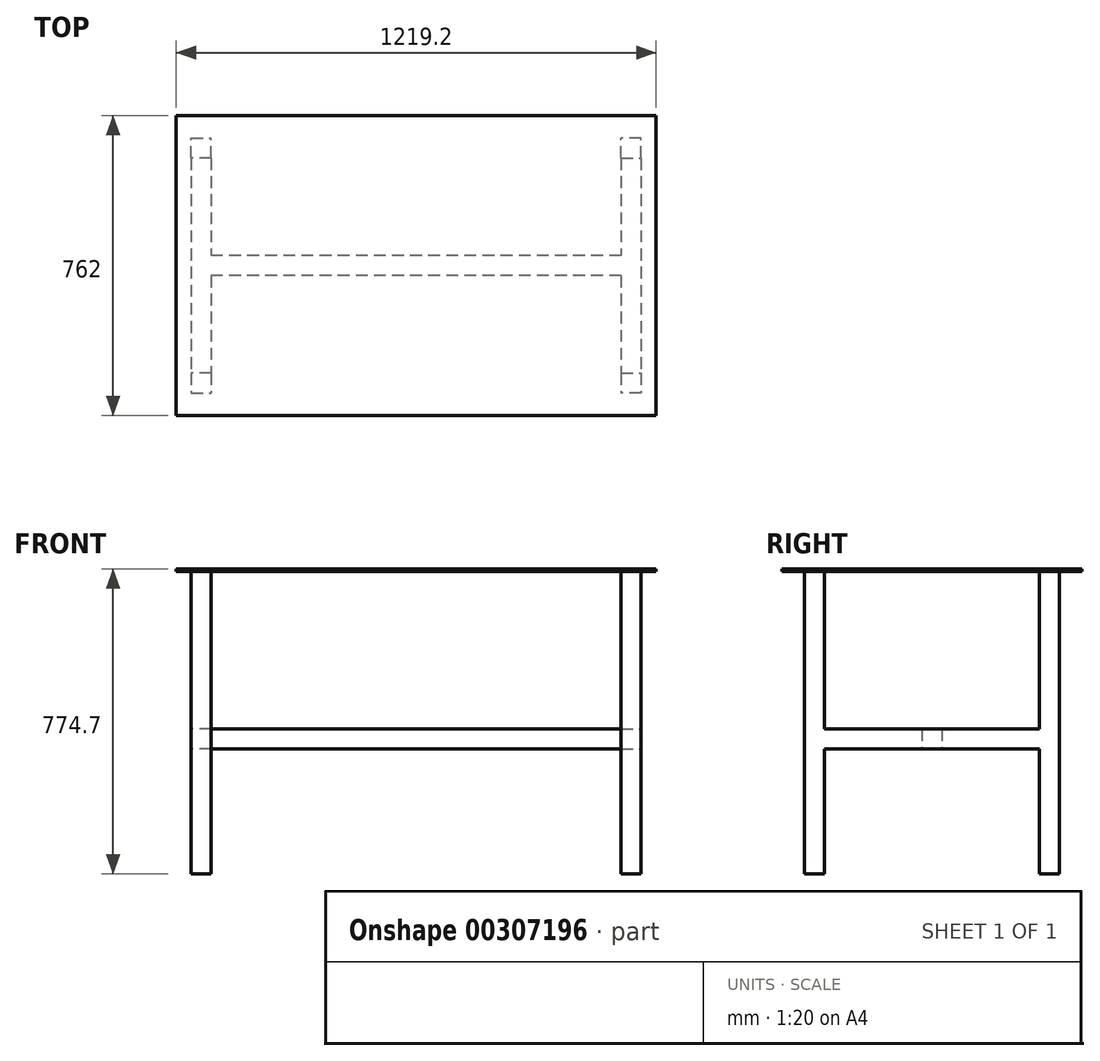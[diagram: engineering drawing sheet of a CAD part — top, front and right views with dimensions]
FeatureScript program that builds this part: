
annotation { "Feature Type Name" : "Feature", "Feature Type Description" : "" }
export const myFeature = defineFeature(function(context is Context, id is Id, definition is map)
    precondition{}
    {
        {
            var Q0;
            Q0=qCreatedBy(makeId("Top.planeOp"),FACE);
            var sketch = newSketch(context, id + "F0", { "sketchPlane" : qUnion([Q0])});
            skLineSegment(sketch, "E0.bottom", {"start": v(-609.6, 381) * mm, "end": v(609.6, 381) * mm});
            skLineSegment(sketch, "E0.top", {"start": v(-609.6, -381) * mm, "end": v(609.6, -381) * mm});
            skLineSegment(sketch, "E0.left", {"start": v(-609.6, 381) * mm, "end": v(-609.6, -381) * mm});
            skLineSegment(sketch, "E0.right", {"start": v(609.6, 381) * mm, "end": v(609.6, -381) * mm});
            skPoint(sketch, "E0.middle", {"position": v(0, 0) * mm});
            skSolve(sketch);
        }
        {
            var Q0;
            Q0 = qSketchRegion(id + "F0", true);
            extrude(context, id + "F1", {"entities" : qUnion([Q0]), "depth" : 6.35 * mm});
        }
        {
            var Q0;
            Q0=makeQuery(id+"F1.opExtrude","CAP_FACE",FACE,{"disambiguationData":[OSD([sQuery(id+"F0.wireOp",EDGE,"E0.bottom"),sQuery(id+"F0.wireOp",EDGE,"E0.top"),sQuery(id+"F0.wireOp",EDGE,"E0.left"),sQuery(id+"F0.wireOp",EDGE,"E0.right")])],"isStart":true});
            var sketch = newSketch(context, id + "F2", { "sketchPlane" : qUnion([Q0])});
            skLineSegment(sketch, "E1.bottom", {"start": v(571.5, -273.05) * mm, "end": v(520.7, -273.05) * mm});
            skLineSegment(sketch, "E1.top", {"start": v(571.5, -323.85) * mm, "end": v(520.7, -323.85) * mm});
            skLineSegment(sketch, "E1.left", {"start": v(571.5, -273.05) * mm, "end": v(571.5, -323.85) * mm});
            skLineSegment(sketch, "E1.right", {"start": v(520.7, -273.05) * mm, "end": v(520.7, -323.85) * mm});
            skLineSegment(sketch, "E2.MirrorCS", {"start": v(-571.5, -273.05) * mm, "end": v(-520.7, -273.05) * mm});
            skLineSegment(sketch, "E3.MirrorCS", {"start": v(-571.5, -323.85) * mm, "end": v(-520.7, -323.85) * mm});
            skLineSegment(sketch, "E4.MirrorCS", {"start": v(-520.7, -273.05) * mm, "end": v(-520.7, -323.85) * mm});
            skLineSegment(sketch, "E5.MirrorCS", {"start": v(-571.5, -273.05) * mm, "end": v(-571.5, -323.85) * mm});
            skLineSegment(sketch, "E6.MirrorCS", {"start": v(571.5, 273.05) * mm, "end": v(571.5, 323.85) * mm});
            skLineSegment(sketch, "E7.MirrorCS", {"start": v(-520.7, 273.05) * mm, "end": v(-520.7, 323.85) * mm});
            skLineSegment(sketch, "E8.MirrorCS", {"start": v(-571.5, 323.85) * mm, "end": v(-520.7, 323.85) * mm});
            skLineSegment(sketch, "E9.MirrorCS", {"start": v(-571.5, 273.05) * mm, "end": v(-520.7, 273.05) * mm});
            skLineSegment(sketch, "E10.MirrorCS", {"start": v(520.7, 273.05) * mm, "end": v(520.7, 323.85) * mm});
            skLineSegment(sketch, "E11.MirrorCS", {"start": v(571.5, 323.85) * mm, "end": v(520.7, 323.85) * mm});
            skLineSegment(sketch, "E12.MirrorCS", {"start": v(-571.5, 273.05) * mm, "end": v(-571.5, 323.85) * mm});
            skLineSegment(sketch, "E13.MirrorCS", {"start": v(571.5, 273.05) * mm, "end": v(520.7, 273.05) * mm});
            skSolve(sketch);
        }
        {
            var Q0;
            Q0 = qSketchRegion(id + "F2", true);
            extrude(context, id + "F3", {"entities" : qUnion([Q0]), "operationType" : NewBodyOperationType.ADD, "depth" : 768.35 * mm});
        }
        {
            var Q0;
            Q0=makeQuery(id+"F3.opExtrude","SWEPT_FACE",FACE,{"disambiguationData":[OSD([sQuery(id+"F2.wireOp",EDGE,"E5.MirrorCS")])]});
            var sketch = newSketch(context, id + "F4", { "sketchPlane" : qUnion([Q0])});
            skLineSegment(sketch, "E14.bottom", {"start": v(-273.05, -400.05) * mm, "end": v(273.05, -400.05) * mm});
            skLineSegment(sketch, "E14.top", {"start": v(-273.05, -450.85) * mm, "end": v(273.05, -450.85) * mm});
            skLineSegment(sketch, "E14.left", {"start": v(-273.05, -400.05) * mm, "end": v(-273.05, -450.85) * mm});
            skLineSegment(sketch, "E14.right", {"start": v(273.05, -400.05) * mm, "end": v(273.05, -450.85) * mm});
            skSolve(sketch);
        }
        {
            var Q0;
            Q0 = qSketchRegion(id + "F4", true);
            extrude(context, id + "F5", {"entities" : qUnion([Q0]), "operationType" : NewBodyOperationType.ADD, "oppositeDirection" : true, "depth" : 50.8 * mm});
        }
        {
            var Q0;
            Q0=makeQuery(id+"F1.opExtrude","SWEPT_BODY",BODY,{"disambiguationData":[OSD([sQuery(id+"F0.wireOp",EDGE,"E0.bottom"),sQuery(id+"F0.wireOp",EDGE,"E0.top"),sQuery(id+"F0.wireOp",EDGE,"E0.left"),sQuery(id+"F0.wireOp",EDGE,"E0.right")])]});
            var Q1;
            Q1=qCreatedBy(makeId("Right.planeOp"),FACE);
            mirror(context, id + "F6", {"operationType" : NewBodyOperationType.ADD, "entities" : qUnion([Q0]), "mirrorPlane" : qUnion([Q1])});
        }
        {
            var Q0;
            Q0=makeQuery(id+"F5.opExtrude","SWEPT_FACE",FACE,{"disambiguationData":[OSD([sQuery(id+"F4.wireOp",EDGE,"E14.top")])]});
            var sketch = newSketch(context, id + "F7", { "sketchPlane" : qUnion([Q0])});
            skLineSegment(sketch, "E15.bottom", {"start": v(-520.7, -25.4) * mm, "end": v(520.7, -25.4) * mm});
            skLineSegment(sketch, "E15.top", {"start": v(-520.7, 25.4) * mm, "end": v(520.7, 25.4) * mm});
            skLineSegment(sketch, "E15.left", {"start": v(-520.7, -25.4) * mm, "end": v(-520.7, 25.4) * mm});
            skLineSegment(sketch, "E15.right", {"start": v(520.7, -25.4) * mm, "end": v(520.7, 25.4) * mm});
            skPoint(sketch, "E15.middle", {"position": v(0, 0) * mm});
            skSolve(sketch);
        }
        {
            var Q0;
            Q0 = qSketchRegion(id + "F7", true);
            var Q1;
            Q1=makeQuery(id+"F5.opExtrude","SWEPT_FACE",FACE,{"disambiguationData":[OSD([sQuery(id+"F4.wireOp",EDGE,"E14.bottom")])]});
            extrude(context, id + "F8", {"entities" : qUnion([Q0]), "operationType" : NewBodyOperationType.ADD, "endBound" : BoundingType.UP_TO_SURFACE, "oppositeDirection" : true, "endBoundEntityFace" : qUnion([Q1]), "depth" : 25.4 * mm});
        }
    });
